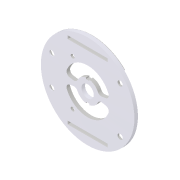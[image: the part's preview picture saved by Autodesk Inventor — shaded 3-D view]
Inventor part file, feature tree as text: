
AUTODESK INVENTOR PART (.ipt)
format: ipt  version: 2018 (Build 220112000, 112)  size: 363,520 bytes
history: native  units: in
note: dims shown in document units (in); Inventor stores cm internally (conversion verified against a paired STEP export)
features: extrude x12, sketch x12, fillet x3, mirror x1, chamfer x1
ambient origin geometry x8: Origin, YZ Plane, XZ Plane, XY Plane, X Axis, Y Axis, Z Axis, Center Point
bodies: Solid1 (feature_tree)
feature tree (29):
  extrude  "Extrusion1"  Depth=0.1181in TaperAngle=0.0deg
  extrude  "Extrusion2"  Depth=0.1181in TaperAngle=0.0deg
  extrude  "Extrusion3"  Depth=0.689in
  extrude  "Extrusion4"  Depth=0.1732in
  fillet  "Fillet1"  Radius=0.5in
  fillet  "Fillet2"  Radius=1.2in
  extrude  "Extrusion5"  Depth=0.75in
  mirror  "Mirror1"
  chamfer  "Chamfer1"  Distance=1.0in
  extrude  "Extrusion6"  Depth=0.125in
  extrude  "Extrusion7"  Depth=1.3in
  extrude  "Extrusion8"  Depth=1.2in
  extrude  "Extrusion9"  Depth=0.0197in TaperAngle=45.0deg
  extrude  "Extrusion10"  Depth=0.5in
  extrude  "Extrusion11"  Depth=0.0256in TaperAngle=0.0deg
  extrude  "Extrusion13"  Depth=0.0256in TaperAngle=0.0deg
  fillet  "Fillet3"  Radius=0.75in
  sketch  "Sketch1"  dims[d0=3.125in d1=0.1181in d2=0.0in]
  sketch  "Sketch2"  dims[d3=0.4125in d4=0.1181in d5=0.0in]
  sketch  "Sketch3"  dims[d6=0.1181in d7=0.689in]
  sketch  "Sketch4"  dims[d8=0.1181in d9=0.0in d10=0.1732in d11=0.5in d12=1.2in]
  sketch  "Sketch6"  dims[d13=1.5in d14=0.75in]
  sketch  "Sketch7"  dims[d15=0.0687in d16=1.0in d17=0.0in]
  sketch  "Sketch8"  dims[d18=0.125in d19=0.125in]
  sketch  "Sketch9"  dims[d20=0.07in d21=1.3in]
  sketch  "Sketch11"  dims[d22=0.65in d23=1.2in]
  sketch  "Sketch12"  dims[d24=0.0984in d25=0.0in d26=0.0197in d27=0.125in d28=45.0deg]
  sketch  "Sketch13"  dims[d29=0.1299in d30=0.5in]
  sketch  "Sketch17"  dims[d31=0.7638in d32=1.0359in d33=0.0in d35=0.0866in d36=0.0in d37=0.75in d38=0.375in d39=0.2953in d40=0.2362in d41=0.2362in d42=0.0866in d43=0.0in d44=0.2362in d45=0.1732in d46=1.0in d47=0.0in d48=2.9003in d50=0.0472in d51=0.1181in d52=0.0591in d53=1.0in d54=0.0in d57=0.2953in d58=0.2953in d59=0.0866in d60=0.0in d67=1.0866in d69=0.1732in d70=0.2362in d72=0.7874in d84=3.125in d85=3.025in d86=45.0deg d87=45.0deg d88=0.0394in d89=0.0in d90=0.0256in d91=1.0866in d92=0.7705in]
